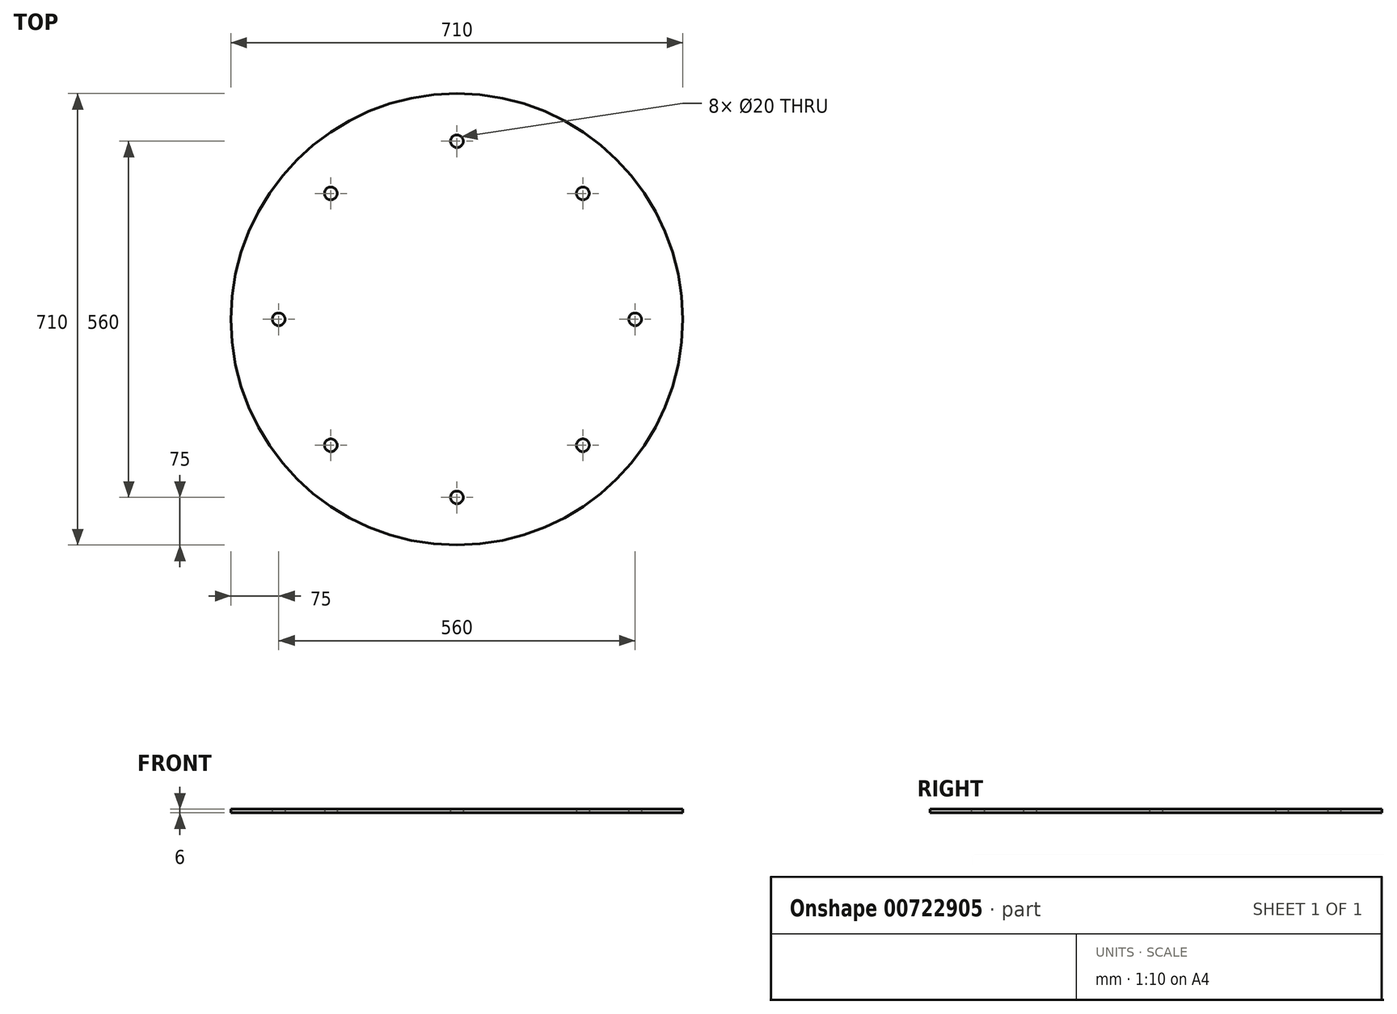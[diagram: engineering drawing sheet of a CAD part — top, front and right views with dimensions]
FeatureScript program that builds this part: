
annotation { "Feature Type Name" : "Feature", "Feature Type Description" : "" }
export const myFeature = defineFeature(function(context is Context, id is Id, definition is map)
    precondition{}
    {
        {
            var Q0;
            Q0=qCreatedBy(makeId("Top.planeOp"),FACE);
            var sketch = newSketch(context, id + "F0", { "sketchPlane" : qUnion([Q0])});
            skCircle(sketch, "E0", {"center": v(0, 0) * mm, "radius": 355 * mm});
            skLineSegment(sketch, "E1", {"start": v(0, 0) * mm, "end": v(280, 0) * mm});
            skLineSegment(sketch, "E2", {"start": v(0, 0) * mm, "end": v(-280, 0) * mm});
            skCircle(sketch, "E3", {"center": v(280, 0) * mm, "radius": 10 * mm});
            skCircle(sketch, "E4", {"center": v(-280, 0) * mm, "radius": 10 * mm});
            skCircle(sketch, "E5.1.0", {"center": v(197.99, 197.99) * mm, "radius": 10 * mm});
            skCircle(sketch, "E5.2.0", {"center": v(0, 280) * mm, "radius": 10 * mm});
            skCircle(sketch, "E5.3.0", {"center": v(-197.99, 197.99) * mm, "radius": 10 * mm});
            skCircle(sketch, "E5.5.0", {"center": v(-197.99, -197.99) * mm, "radius": 10 * mm});
            skCircle(sketch, "E5.6.0", {"center": v(0, -280) * mm, "radius": 10 * mm});
            skCircle(sketch, "E5.7.0", {"center": v(197.99, -197.99) * mm, "radius": 10 * mm});
            skSolve(sketch);
        }
        {
            var Q0;
            Q0=makeQuery(id+"F0.imprint","IMPRINT",FACE,{"disambiguationData":[TD([[makeQuery(id+"F0.imprint","IMPRINT",EDGE,{"derivedFrom":sQuery(id+"F0.wireOp",EDGE,"E0")}),1.0]])]});
            extrude(context, id + "F1", {"entities" : qUnion([Q0]), "depth" : 6 * mm, "offsetDistance" : 25 * mm});
        }
    });
